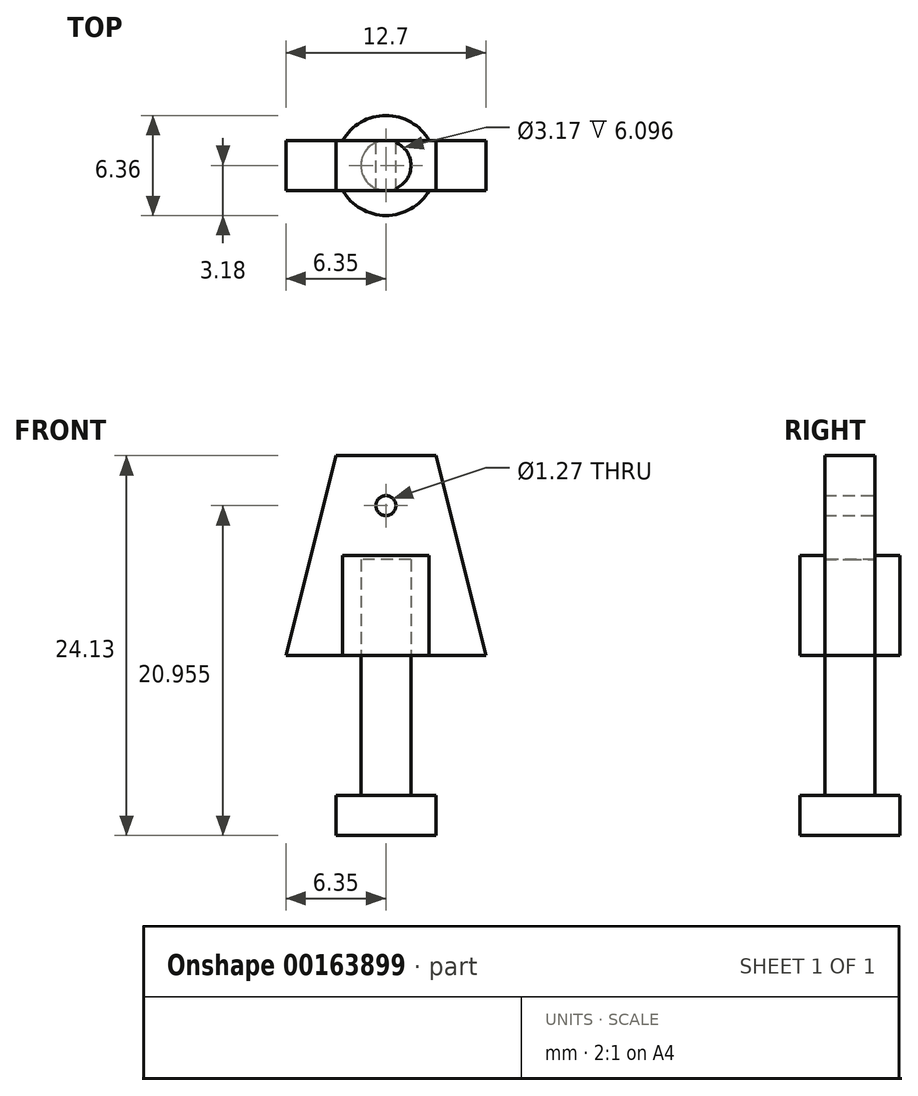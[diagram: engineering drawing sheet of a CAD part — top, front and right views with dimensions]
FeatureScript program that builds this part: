
annotation { "Feature Type Name" : "Feature", "Feature Type Description" : "" }
export const myFeature = defineFeature(function(context is Context, id is Id, definition is map)
    precondition{}
    {
        {
            var Q0;
            Q0=qCreatedBy(makeId("Front.planeOp"),FACE);
            var sketch = newSketch(context, id + "F0", { "sketchPlane" : qUnion([Q0])});
            skLineSegment(sketch, "E0", {"start": v(-6.35, 0) * mm, "end": v(6.35, 0) * mm});
            skLineSegment(sketch, "E1", {"start": v(6.35, 0) * mm, "end": v(3.17, 12.7) * mm});
            skLineSegment(sketch, "E2", {"start": v(3.18, 12.7) * mm, "end": v(-3.18, 12.7) * mm});
            skLineSegment(sketch, "E3", {"start": v(-3.18, 12.7) * mm, "end": v(-6.35, 0) * mm});
            skLineSegment(sketch, "E4", {"start": v(0, 0) * mm, "end": v(0, 9.52) * mm, "construction": true});
            skLineSegment(sketch, "E5", {"start": v(0, 12.7) * mm, "end": v(0, 9.52) * mm, "construction": true});
            skCircle(sketch, "E6", {"center": v(0, 9.52) * mm, "radius": 0.64 * mm});
            skSolve(sketch);
        }
        {
            var Q0;
            Q0 = qSketchRegion(id + "F0", true);
            extrude(context, id + "F1", {"entities" : qUnion([Q0]), "depth" : 1.59 * mm, "hasSecondDirection" : true, "secondDirectionOppositeDirection" : true, "secondDirectionDepth" : 1.59 * mm});
        }
        {
            var Q0;
            Q0=qCreatedBy(makeId("Top.planeOp"),FACE);
            var sketch = newSketch(context, id + "F2", { "sketchPlane" : qUnion([Q0])});
            skCircle(sketch, "E7", {"center": v(0, 0) * mm, "radius": 3.18 * mm});
            skCircle(sketch, "E8", {"center": v(0, 0) * mm, "radius": 1.59 * mm});
            skSolve(sketch);
        }
        {
            var Q0;
            Q0=makeQuery(id+"F2.imprint","IMPRINT",FACE,{"disambiguationData":[TD([[makeQuery(id+"F2.imprint","IMPRINT",EDGE,{"derivedFrom":sQuery(id+"F2.wireOp",EDGE,"E7")}),1.0]])]});
            extrude(context, id + "F3", {"entities" : qUnion([Q0]), "operationType" : NewBodyOperationType.ADD, "depth" : 6.35 * mm});
        }
        {
            var Q0;
            Q0=makeQuery(id+"F2.imprint","IMPRINT",FACE,{"disambiguationData":[TD([[makeQuery(id+"F2.imprint","IMPRINT",EDGE,{"derivedFrom":sQuery(id+"F2.wireOp",EDGE,"E8")}),1.0]])]});
            extrude(context, id + "F4", {"entities" : qUnion([Q0]), "operationType" : NewBodyOperationType.REMOVE, "depth" : 6.1 * mm});
        }
        {
            var Q0;
            Q0=makeQuery(id+"F2.imprint","IMPRINT",FACE,{"disambiguationData":[TD([[makeQuery(id+"F2.imprint","IMPRINT",EDGE,{"derivedFrom":sQuery(id+"F2.wireOp",EDGE,"E8")}),1.0]])]});
            extrude(context, id + "F5", {"entities" : qUnion([Q0]), "oppositeDirection" : true, "depth" : 11.43 * mm});
        }
        {
            var Q0;
            Q0=makeQuery(id+"F2.imprint","IMPRINT",FACE,{"disambiguationData":[TD([[makeQuery(id+"F2.imprint","IMPRINT",EDGE,{"derivedFrom":sQuery(id+"F2.wireOp",EDGE,"E7")}),1.0]])]});
            extrude(context, id + "F6", {"entities" : qUnion([Q0]), "operationType" : NewBodyOperationType.ADD, "oppositeDirection" : true, "depth" : 11.43 * mm, "hasSecondDirection" : true, "secondDirectionOppositeDirection" : true, "secondDirectionDepth" : 8.9 * mm});
        }
    });
